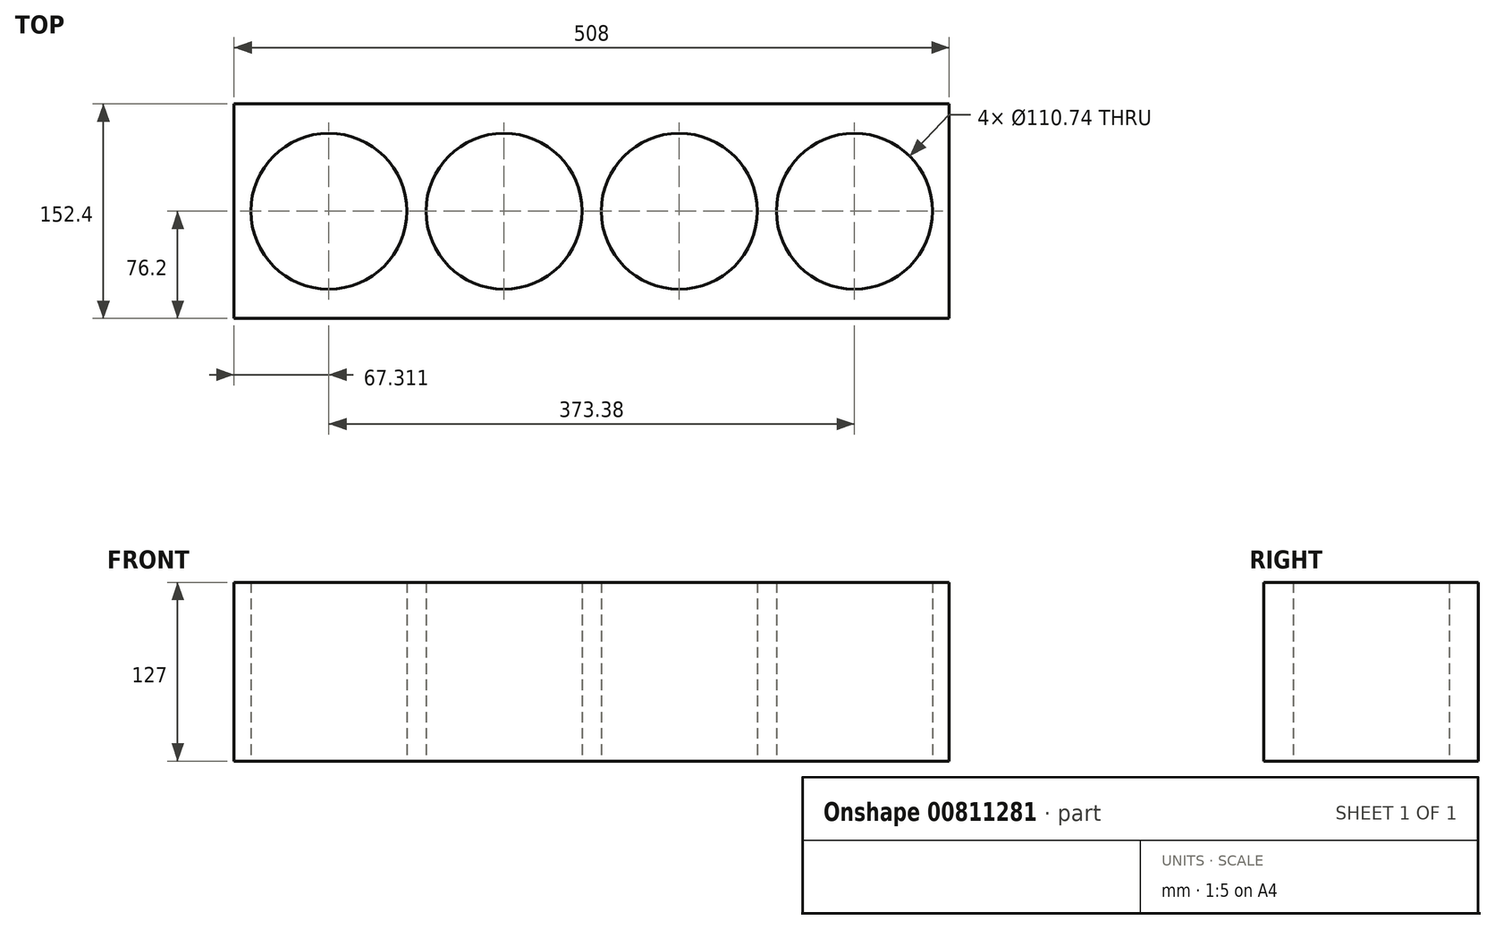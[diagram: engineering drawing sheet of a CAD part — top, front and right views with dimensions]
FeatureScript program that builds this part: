
annotation { "Feature Type Name" : "Feature", "Feature Type Description" : "" }
export const myFeature = defineFeature(function(context is Context, id is Id, definition is map)
    precondition{}
    {
        {
            var Q0;
            Q0=qCreatedBy(makeId("Top.planeOp"),FACE);
            var sketch = newSketch(context, id + "F0", { "sketchPlane" : qUnion([Q0])});
            skCircle(sketch, "E0", {"center": v(-297.64, 0) * mm, "radius": 55.37 * mm});
            skCircle(sketch, "E1.1.0.0", {"center": v(-173.18, 0) * mm, "radius": 55.37 * mm});
            skCircle(sketch, "E1.2.0.0", {"center": v(-48.72, 0) * mm, "radius": 55.37 * mm});
            skCircle(sketch, "E1.3.0.0", {"center": v(75.74, 0) * mm, "radius": 55.37 * mm});
            skLineSegment(sketch, "E1.direction1", {"start": v(-297.64, 0) * mm, "end": v(-173.18, 0) * mm, "construction": true});
            skLineSegment(sketch, "E2", {"start": v(-297.64, 0) * mm, "end": v(75.74, 0) * mm, "construction": true});
            skLineSegment(sketch, "E3.bottom", {"start": v(143.05, -76.2) * mm, "end": v(-364.95, -76.2) * mm});
            skLineSegment(sketch, "E3.top", {"start": v(143.05, 76.2) * mm, "end": v(-364.95, 76.2) * mm});
            skLineSegment(sketch, "E3.left", {"start": v(143.05, -76.2) * mm, "end": v(143.05, 76.2) * mm});
            skLineSegment(sketch, "E3.right", {"start": v(-364.95, -76.2) * mm, "end": v(-364.95, 76.2) * mm});
            skPoint(sketch, "E3.middle", {"position": v(-110.95, 0) * mm});
            skSolve(sketch);
        }
        {
            var Q0;
            Q0=makeQuery(id+"F0.imprint","IMPRINT",FACE,{"disambiguationData":[TD([[makeQuery(id+"F0.imprint","IMPRINT",EDGE,{"derivedFrom":sQuery(id+"F0.wireOp",EDGE,"E0")}),-1.0]])]});
            extrude(context, id + "F1", {"entities" : qUnion([Q0]), "depth" : 127 * mm, "offsetDistance" : 25.4 * mm});
        }
    });
